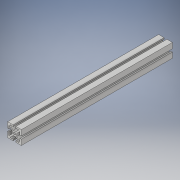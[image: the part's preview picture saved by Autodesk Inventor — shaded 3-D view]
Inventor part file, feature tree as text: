
AUTODESK INVENTOR PART (.ipt)
format: ipt  version: 2018 (Build 220112000, 112)  size: 153,600 bytes
history: native  units: mm
features: extrude x1, sketch x1
ambient origin geometry x8: Origin, YZ Plane, XZ Plane, XY Plane, X Axis, Y Axis, Z Axis, Center Point
bodies: Volumenkörper1 (feature_tree)
feature tree (2):
  extrude  "Extrusion1"  Depth=3.0mm
  sketch  "Skizze1"  dims[d0=3.0mm d1=3.0mm d2=0.5mm d3=1.0mm d4=1.0mm d5=1.2mm d6=1.2mm d7=1.2mm d8=1.2mm d9=0.3mm d10=0.15mm d11=0.15mm d12=0.15mm d13=0.15mm d14=33.0mm d15=0.0mm]
